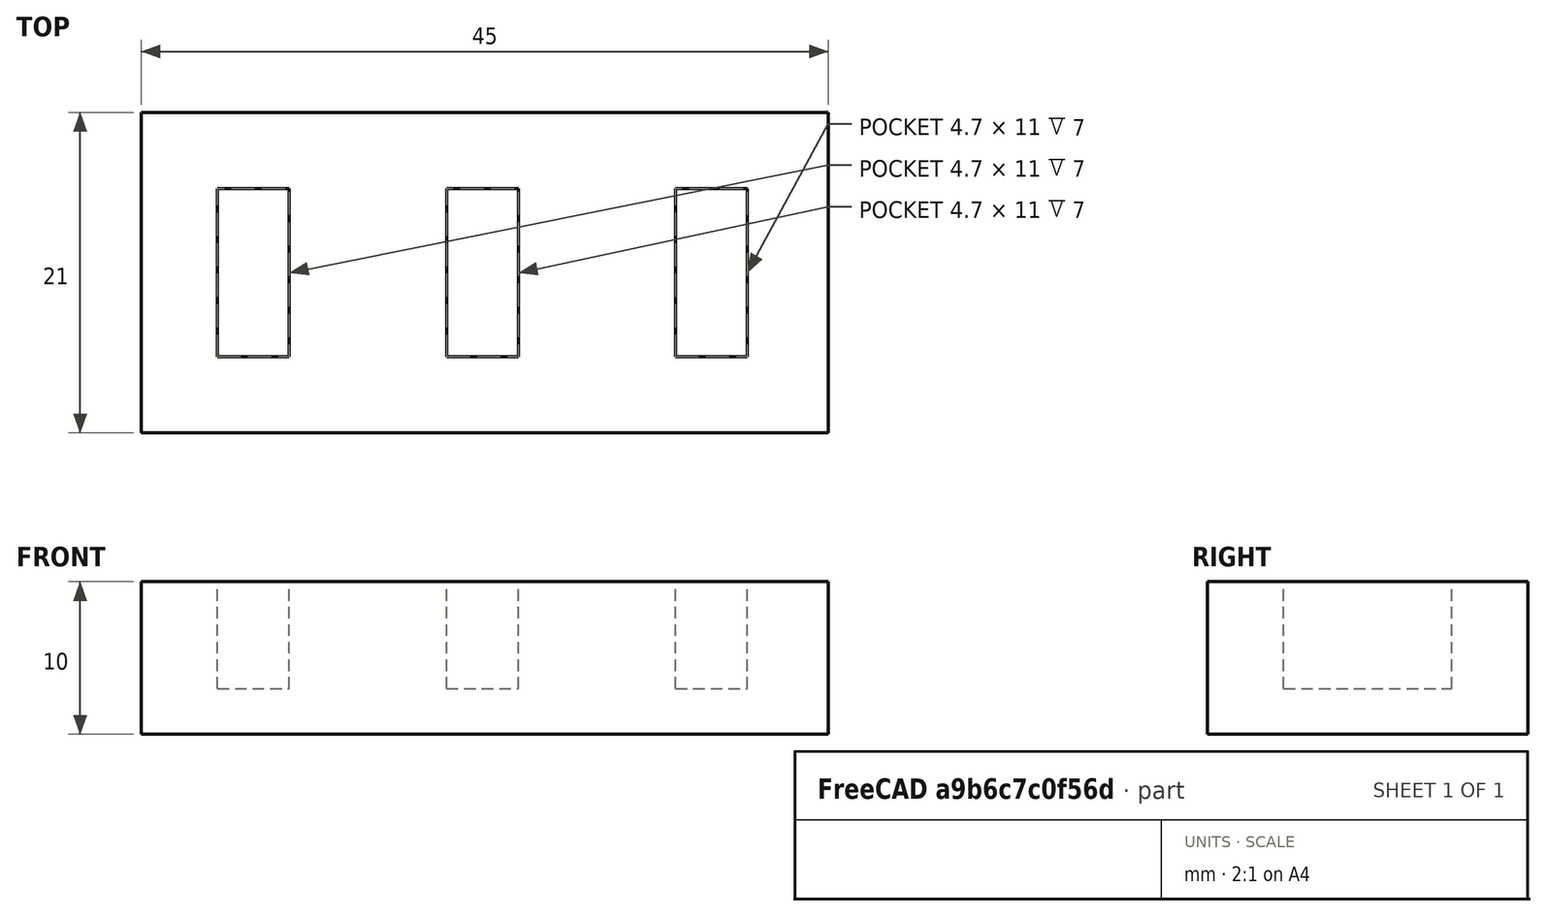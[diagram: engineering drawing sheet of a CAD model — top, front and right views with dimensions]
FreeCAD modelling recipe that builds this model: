
FCSTD DOCUMENT  (FreeCAD 0.18.4R)
Label: tutorial_freecad_ex08_a
License: All rights reserved
LicenseURL: http://en.wikipedia.org/wiki/All_rights_reserved
objects: Part::Box×4, Part::MultiFuse×1, Part::Cut×1
note: 6 computed .brp shape members not serialized (recipe doc carries the construction recipe); baked Part::Feature solids carry a one-line shape summary decoded from their .brp

FEATURE [Part::Box] Box  label="ranura_001"
  AttacherType = Attacher::AttachEngine3D
  Height = 12
  Length = 4.7
  Width = 11
FEATURE [Part::Box] Box001  label="ranura_002"
  AttacherType = Attacher::AttachEngine3D
  Height = 12
  Length = 4.7
  Placement = pos=(15,0,0) rot=(0,0,1;0rad)
  Width = 11
FEATURE [Part::Box] Box002  label="ranura_003"
  AttacherType = Attacher::AttachEngine3D
  Height = 12
  Length = 4.7
  Placement = pos=(30,0,0) rot=(0,0,1;0rad)
  Width = 11
FEATURE [Part::MultiFuse] Fusion  label="ranuras"
  Placement = pos=(5,5,3) rot=(0,0,1;0rad)
  Refine = true
  Shapes = -> [Box,Box001,Box002]
FEATURE [Part::Box] Box003  label="base"
  AttacherType = Attacher::AttachEngine3D
  Height = 10
  Length = 45
  Width = 21
FEATURE [Part::Cut] Cut  label="porta-pendrives"
  Base = -> Box003
  Refine = true
  Tool = -> Fusion
